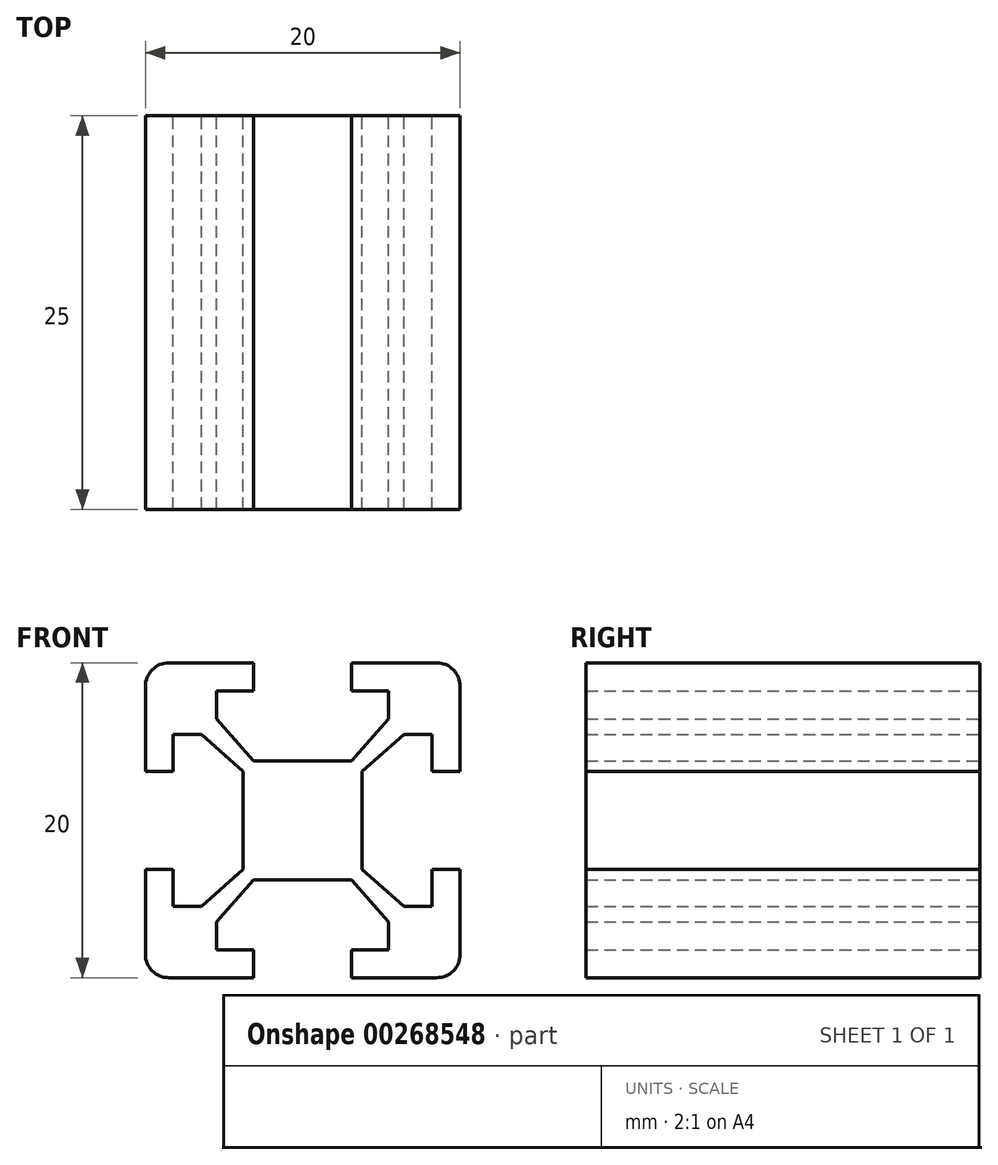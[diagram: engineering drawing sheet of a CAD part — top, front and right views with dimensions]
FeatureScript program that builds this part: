
annotation { "Feature Type Name" : "Feature", "Feature Type Description" : "" }
export const myFeature = defineFeature(function(context is Context, id is Id, definition is map)
    precondition{}
    {
        {
            var Q0;
            Q0=qCreatedBy(makeId("Front.planeOp"),FACE);
            var sketch = newSketch(context, id + "F0", { "sketchPlane" : qUnion([Q0])});
            skLineSegment(sketch, "E0.bottom", {"start": v(10, 10) * mm, "end": v(-10, 10) * mm});
            skLineSegment(sketch, "E0.top", {"start": v(10, -10) * mm, "end": v(-10, -10) * mm});
            skLineSegment(sketch, "E0.left", {"start": v(10, 10) * mm, "end": v(10, -10) * mm});
            skLineSegment(sketch, "E0.right", {"start": v(-10, 10) * mm, "end": v(-10, -10) * mm});
            skPoint(sketch, "E0.middle", {"position": v(0, 0) * mm});
            skLineSegment(sketch, "E1", {"start": v(3.11, 10) * mm, "end": v(3.11, 8.22) * mm});
            skLineSegment(sketch, "E2", {"start": v(3.11, 8.22) * mm, "end": v(5.46, 8.22) * mm});
            skLineSegment(sketch, "E3", {"start": v(5.46, 8.22) * mm, "end": v(5.46, 6.44) * mm});
            skLineSegment(sketch, "E4", {"start": v(5.46, 6.44) * mm, "end": v(3.11, 3.78) * mm});
            skLineSegment(sketch, "E5", {"start": v(3.11, 3.78) * mm, "end": v(0, 3.78) * mm});
            skLineSegment(sketch, "E6.MirrorCS", {"start": v(-3.11, 3.78) * mm, "end": v(0, 3.78) * mm});
            skLineSegment(sketch, "E7.MirrorCS", {"start": v(-5.46, 6.44) * mm, "end": v(-3.11, 3.78) * mm});
            skLineSegment(sketch, "E8.MirrorCS", {"start": v(-3.11, 10) * mm, "end": v(-3.11, 8.22) * mm});
            skLineSegment(sketch, "E9.MirrorCS", {"start": v(-5.46, 8.22) * mm, "end": v(-5.46, 6.44) * mm});
            skLineSegment(sketch, "E10.MirrorCS", {"start": v(-3.11, 8.22) * mm, "end": v(-5.46, 8.22) * mm});
            skLineSegment(sketch, "E11.1.0", {"start": v(-10, 3.11) * mm, "end": v(-8.22, 3.11) * mm});
            skLineSegment(sketch, "E11.1.1", {"start": v(-8.22, 3.11) * mm, "end": v(-8.22, 5.46) * mm});
            skLineSegment(sketch, "E11.1.2", {"start": v(-8.22, 5.46) * mm, "end": v(-6.44, 5.46) * mm});
            skLineSegment(sketch, "E11.1.3", {"start": v(-6.44, 5.46) * mm, "end": v(-3.78, 3.11) * mm});
            skLineSegment(sketch, "E11.1.4", {"start": v(-3.78, 3.11) * mm, "end": v(-3.78, 0) * mm});
            skLineSegment(sketch, "E11.1.5", {"start": v(-3.78, -3.11) * mm, "end": v(-3.78, 0) * mm});
            skLineSegment(sketch, "E11.1.6", {"start": v(-6.44, -5.46) * mm, "end": v(-3.78, -3.11) * mm});
            skLineSegment(sketch, "E11.1.7", {"start": v(-10, -3.11) * mm, "end": v(-8.22, -3.11) * mm});
            skLineSegment(sketch, "E11.1.8", {"start": v(-8.22, -5.46) * mm, "end": v(-6.44, -5.46) * mm});
            skLineSegment(sketch, "E11.1.9", {"start": v(-8.22, -3.11) * mm, "end": v(-8.22, -5.46) * mm});
            skLineSegment(sketch, "E11.2.0", {"start": v(-3.11, -10) * mm, "end": v(-3.11, -8.22) * mm});
            skLineSegment(sketch, "E11.2.1", {"start": v(-3.11, -8.22) * mm, "end": v(-5.46, -8.22) * mm});
            skLineSegment(sketch, "E11.2.2", {"start": v(-5.46, -8.22) * mm, "end": v(-5.46, -6.44) * mm});
            skLineSegment(sketch, "E11.2.3", {"start": v(-5.46, -6.44) * mm, "end": v(-3.11, -3.78) * mm});
            skLineSegment(sketch, "E11.2.4", {"start": v(-3.11, -3.78) * mm, "end": v(0, -3.78) * mm});
            skLineSegment(sketch, "E11.2.5", {"start": v(3.11, -3.78) * mm, "end": v(0, -3.78) * mm});
            skLineSegment(sketch, "E11.2.6", {"start": v(5.46, -6.44) * mm, "end": v(3.11, -3.78) * mm});
            skLineSegment(sketch, "E11.2.7", {"start": v(3.11, -10) * mm, "end": v(3.11, -8.22) * mm});
            skLineSegment(sketch, "E11.2.8", {"start": v(5.46, -8.22) * mm, "end": v(5.46, -6.44) * mm});
            skLineSegment(sketch, "E11.2.9", {"start": v(3.11, -8.22) * mm, "end": v(5.46, -8.22) * mm});
            skLineSegment(sketch, "E11.3.0", {"start": v(10, -3.11) * mm, "end": v(8.22, -3.11) * mm});
            skLineSegment(sketch, "E11.3.1", {"start": v(8.22, -3.11) * mm, "end": v(8.22, -5.46) * mm});
            skLineSegment(sketch, "E11.3.2", {"start": v(8.22, -5.46) * mm, "end": v(6.44, -5.46) * mm});
            skLineSegment(sketch, "E11.3.3", {"start": v(6.44, -5.46) * mm, "end": v(3.78, -3.11) * mm});
            skLineSegment(sketch, "E11.3.4", {"start": v(3.78, -3.11) * mm, "end": v(3.78, 0) * mm});
            skLineSegment(sketch, "E11.3.5", {"start": v(3.78, 3.11) * mm, "end": v(3.78, 0) * mm});
            skLineSegment(sketch, "E11.3.6", {"start": v(6.44, 5.46) * mm, "end": v(3.78, 3.11) * mm});
            skLineSegment(sketch, "E11.3.7", {"start": v(10, 3.11) * mm, "end": v(8.22, 3.11) * mm});
            skLineSegment(sketch, "E11.3.8", {"start": v(8.22, 5.46) * mm, "end": v(6.44, 5.46) * mm});
            skLineSegment(sketch, "E11.3.9", {"start": v(8.22, 3.11) * mm, "end": v(8.22, 5.46) * mm});
            skSolve(sketch);
        }
        {
            var Q0;
            {var subQ12=sQuery(id+"F0.wireOp",EDGE,"E1");Q0=makeQuery(id+"F0.imprint","IMPRINT",FACE,{"disambiguationData":[TD([[makeQuery(id+"F0.imprint","IMPRINT",EDGE,{"derivedFrom":subQ12}),1.0]])]});}
            extrude(context, id + "F1", {"entities" : qUnion([Q0]), "depth" : 25 * mm});
        }
        {
            var Q0;
            Q0=makeQuery(id+"F1.opExtrude","SWEPT_EDGE",EDGE,{"disambiguationData":[OSD([sQuery(id+"F0.wireOp",EDGE,"E0.bottom"),sQuery(id+"F0.wireOp",EDGE,"E0.right")])]});
            var Q1;
            Q1=makeQuery(id+"F1.opExtrude","SWEPT_EDGE",EDGE,{"disambiguationData":[OSD([sQuery(id+"F0.wireOp",EDGE,"E0.bottom"),sQuery(id+"F0.wireOp",EDGE,"E0.left")])]});
            var Q2;
            Q2=makeQuery(id+"F1.opExtrude","SWEPT_EDGE",EDGE,{"disambiguationData":[OSD([sQuery(id+"F0.wireOp",EDGE,"E0.top"),sQuery(id+"F0.wireOp",EDGE,"E0.left")])]});
            var Q3;
            Q3=makeQuery(id+"F1.opExtrude","SWEPT_EDGE",EDGE,{"disambiguationData":[OSD([sQuery(id+"F0.wireOp",EDGE,"E0.top"),sQuery(id+"F0.wireOp",EDGE,"E0.right")])]});
            fillet(context, id + "F2", {"entities" : qUnion([Q0, Q1, Q2, Q3]), "radius" : 1.5 * mm, "tangentPropagation" : true, "allowEdgeOverflow" : false});
        }
        {
            var Q0;
            Q0=makeQuery(id+"F1.opExtrude","SWEPT_BODY",BODY,{"disambiguationData":[OSD([sQuery(id+"F0.wireOp",EDGE,"E0.bottom"),sQuery(id+"F0.wireOp",EDGE,"E0.top"),sQuery(id+"F0.wireOp",EDGE,"E0.left"),sQuery(id+"F0.wireOp",EDGE,"E0.right"),sQuery(id+"F0.wireOp",EDGE,"E1"),sQuery(id+"F0.wireOp",EDGE,"E2"),sQuery(id+"F0.wireOp",EDGE,"E3"),sQuery(id+"F0.wireOp",EDGE,"E4"),sQuery(id+"F0.wireOp",EDGE,"E5"),sQuery(id+"F0.wireOp",EDGE,"E6.MirrorCS"),sQuery(id+"F0.wireOp",EDGE,"E7.MirrorCS"),sQuery(id+"F0.wireOp",EDGE,"E8.MirrorCS"),sQuery(id+"F0.wireOp",EDGE,"E9.MirrorCS"),sQuery(id+"F0.wireOp",EDGE,"E10.MirrorCS"),sQuery(id+"F0.wireOp",EDGE,"E11.1.0"),sQuery(id+"F0.wireOp",EDGE,"E11.1.1"),sQuery(id+"F0.wireOp",EDGE,"E11.1.2"),sQuery(id+"F0.wireOp",EDGE,"E11.1.3"),sQuery(id+"F0.wireOp",EDGE,"E11.1.4"),sQuery(id+"F0.wireOp",EDGE,"E11.1.5"),sQuery(id+"F0.wireOp",EDGE,"E11.1.6"),sQuery(id+"F0.wireOp",EDGE,"E11.1.7"),sQuery(id+"F0.wireOp",EDGE,"E11.1.8"),sQuery(id+"F0.wireOp",EDGE,"E11.1.9"),sQuery(id+"F0.wireOp",EDGE,"E11.2.0"),sQuery(id+"F0.wireOp",EDGE,"E11.2.1"),sQuery(id+"F0.wireOp",EDGE,"E11.2.2"),sQuery(id+"F0.wireOp",EDGE,"E11.2.3"),sQuery(id+"F0.wireOp",EDGE,"E11.2.4"),sQuery(id+"F0.wireOp",EDGE,"E11.2.5"),sQuery(id+"F0.wireOp",EDGE,"E11.2.6"),sQuery(id+"F0.wireOp",EDGE,"E11.2.7"),sQuery(id+"F0.wireOp",EDGE,"E11.2.8"),sQuery(id+"F0.wireOp",EDGE,"E11.2.9"),sQuery(id+"F0.wireOp",EDGE,"E11.3.0"),sQuery(id+"F0.wireOp",EDGE,"E11.3.1"),sQuery(id+"F0.wireOp",EDGE,"E11.3.2"),sQuery(id+"F0.wireOp",EDGE,"E11.3.3"),sQuery(id+"F0.wireOp",EDGE,"E11.3.4"),sQuery(id+"F0.wireOp",EDGE,"E11.3.5"),sQuery(id+"F0.wireOp",EDGE,"E11.3.6"),sQuery(id+"F0.wireOp",EDGE,"E11.3.7"),sQuery(id+"F0.wireOp",EDGE,"E11.3.8"),sQuery(id+"F0.wireOp",EDGE,"E11.3.9")])]});
            transform(context, id + "F3", {"entities" : qUnion([Q0]), "transformType" : TransformType.TRANSLATION_3D, "dx" : 0 * mm, "dy" : 0 * mm, "dz" : 0 * mm, "makeCopy" : true});
        }
    });
